# Revit family: CENTUM Dachdurchführung 88,9 m.Massivanschluss, L=300 - 500mm
name_source: partatom
category: HLS-Bauteile
units: mm (PartAtom-declared; Revit-internal decimal feet)

## family parameters
Arbeitsebenenbasiert = Ja
Beim Laden mit Abzugskörper schneiden = Nein
Bemaßung runder Anschluss = Durchmesser verwenden
Beschriftungsausrichtung beibehalten = Nein
Gemeinsam genutzt = Ja
Immer vertikal = Nein
Raumberechnungspunkt = Nein
Teiletyp = Normal

## types (5) — shared parameters
Abmessung Grundplatte = 220x220x12 mm
Ausführung = ohne Höhenverstellung
Breite Platte = 220 mm  [stored 0.721785 ft]
Fabrikat = MEFA
Firma = MEFA Befestigungs- und Montagesysteme GmbH
Kurztext1 = Dachdurchführung CENTUM
Länge Platte = 220 mm  [stored 0.721785 ft]
Massivanschluss = TL-XL Massivanschluss hängend : Massivanschluss XL100 hängend (9000597)
Material = Stahl
Materialname = S235
Mengeneinheit = St
Oberflaeche = feuerstückverzinkt
Platte = Platte 220x220x12 18x27
Profil = CENTUM
Profiltyp = XL100
Stärke Platte = 12 mm  [stored 0.0393701 ft]
Vorgabe-Ansicht = 1219 mm
max. zul. Last Druck = 0.00 kN
vpe = 1
zero-valued in all types: Sicherheitsfaktor, max. Profilhöhe

## per-type parameters (varying)
| type | Artikelnummer | EAN | Gewicht | Gewicht pro Bauteil | Kurztext2 | L | Länge | Länge 1 | Rohrlänge |
| CENTUM Dachdurchführung 88,9 XL100 m.Massivanschluss L= 350 | 166210002 | 4250928463456 | 9.18 kg | 9.18 kg | für XL100 350 mm ohne Höhenverstellung | 350 mm  [stored 1.14829 ft] | 350 mm  [stored 1.14829 ft] | 368 mm | Rohre 88.9x3.2 300 bis 500 : Rohr  88,9/3,2 L= 350 (00096831/0350) |
| CENTUM Dachdurchführung 88,9 XL100 m.Massivanschluss L= 400 | 166210003 | 4250928463463 | 9.57 kg | 9.57 kg | für XL100 400 mm ohne Höhenverstellung | 400 mm  [stored 1.31234 ft] | 400 mm  [stored 1.31234 ft] | 418 mm | Rohre 88.9x3.2 300 bis 500 : Rohr  88,9/3,2 L= 400 (00096831/0400) |
| CENTUM Dachdurchführung 88,9 XL100 m.Massivanschluss L= 450 | 166210004 | 4250928463470 | 9.97 kg | 9.97 kg | für XL100 450 mm ohne Höhenverstellung | 450 mm  [stored 1.47638 ft] | 450 mm  [stored 1.47638 ft] | 468 mm | Rohre 88.9x3.2 300 bis 500 : Rohr  88,9/3,2 L= 450 (00096831/0450) |
| CENTUM Dachdurchführung 88,9 XL100 m.Massivanschluss L= 500 | 166210005 | 4250928463487 | 10.36 kg | 10.36 kg | für XL100 500 mm ohne Höhenverstellung | 500 mm  [stored 1.64042 ft] | 500 mm  [stored 1.64042 ft] | 518 mm | Rohre 88.9x3.2 300 bis 500 : Rohr  88,9/3,2 L= 500 (00096831/0500) |
| CENTUM Dachdurchführung 88,9 XL100 m.Massivanschluss L= 300 | 166210001 | 4250928463449 | 8.79 kg | 8.79 kg | für XL100 300 mm ohne Höhenverstellung | 300 mm  [stored 0.984252 ft] | 300 mm  [stored 0.984252 ft] | 318 mm | Rohre 88.9x3.2 300 bis 500 : Rohr  88,9/3,2 L= 300 (00096831/0300) |

note: [stored X ft] marks values corroborated as IEEE doubles in the binary element streams (Revit-internal decimal feet)
